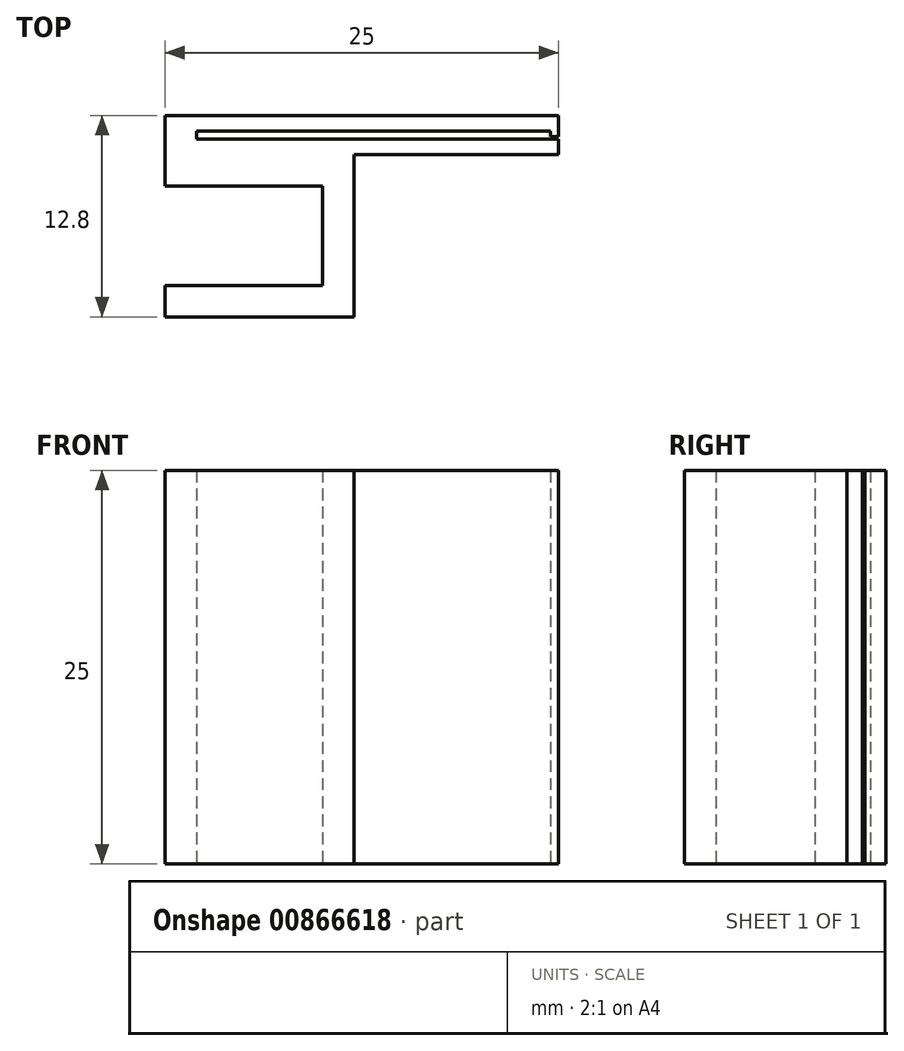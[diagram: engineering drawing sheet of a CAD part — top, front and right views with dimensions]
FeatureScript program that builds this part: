
annotation { "Feature Type Name" : "Feature", "Feature Type Description" : "" }
export const myFeature = defineFeature(function(context is Context, id is Id, definition is map)
    precondition{}
    {
        {
            var Q0;
            Q0=qCreatedBy(makeId("Top.planeOp"),FACE);
            var sketch = newSketch(context, id + "F0", { "sketchPlane" : qUnion([Q0])});
            skLineSegment(sketch, "E0.bottom", {"start": v(-10, 5.15) * mm, "end": v(2, 5.15) * mm});
            skLineSegment(sketch, "E0.top", {"start": v(-10, 3.15) * mm, "end": v(2, 3.15) * mm});
            skLineSegment(sketch, "E0.left", {"start": v(-10, 5.15) * mm, "end": v(-10, 3.15) * mm});
            skLineSegment(sketch, "E0.right", {"start": v(2, 5.15) * mm, "end": v(2, 3.15) * mm});
            skLineSegment(sketch, "E1.bottom", {"start": v(-10, -3.15) * mm, "end": v(2, -3.15) * mm});
            skLineSegment(sketch, "E1.top", {"start": v(-10, -5.15) * mm, "end": v(2, -5.15) * mm});
            skLineSegment(sketch, "E1.left", {"start": v(-10, -3.15) * mm, "end": v(-10, -5.15) * mm});
            skLineSegment(sketch, "E1.right", {"start": v(2, -3.15) * mm, "end": v(2, -5.15) * mm});
            skLineSegment(sketch, "E2.bottom", {"start": v(0, 3.15) * mm, "end": v(2, 3.15) * mm});
            skLineSegment(sketch, "E2.top", {"start": v(0, -3.15) * mm, "end": v(2, -3.15) * mm});
            skLineSegment(sketch, "E2.left", {"start": v(0, 3.15) * mm, "end": v(0, -3.15) * mm});
            skLineSegment(sketch, "E2.right", {"start": v(2, 3.15) * mm, "end": v(2, -3.15) * mm});
            skLineSegment(sketch, "E3", {"start": v(-10, 5.15) * mm, "end": v(15, 5.15) * mm});
            skLineSegment(sketch, "E4", {"start": v(15, 5.15) * mm, "end": v(15, 6.15) * mm});
            skLineSegment(sketch, "E5", {"start": v(15, 6.15) * mm, "end": v(-10, 6.15) * mm});
            skLineSegment(sketch, "E6", {"start": v(-10, 6.15) * mm, "end": v(-10, 5.15) * mm});
            skLineSegment(sketch, "E7.bottom", {"start": v(-10, 6.15) * mm, "end": v(-8, 6.15) * mm});
            skLineSegment(sketch, "E7.top", {"start": v(-10, 6.65) * mm, "end": v(-8, 6.65) * mm});
            skLineSegment(sketch, "E7.left", {"start": v(-10, 6.15) * mm, "end": v(-10, 6.65) * mm});
            skLineSegment(sketch, "E7.right", {"start": v(-8, 6.15) * mm, "end": v(-8, 6.65) * mm});
            skLineSegment(sketch, "E8.bottom", {"start": v(-10, 6.65) * mm, "end": v(15, 6.65) * mm});
            skLineSegment(sketch, "E8.top", {"start": v(-10, 7.65) * mm, "end": v(15, 7.65) * mm});
            skLineSegment(sketch, "E8.left", {"start": v(-10, 6.65) * mm, "end": v(-10, 7.65) * mm});
            skLineSegment(sketch, "E8.right", {"start": v(15, 6.65) * mm, "end": v(15, 7.65) * mm});
            skLineSegment(sketch, "E9.bottom", {"start": v(15, 6.65) * mm, "end": v(14.5, 6.65) * mm});
            skLineSegment(sketch, "E9.top", {"start": v(15, 6.3) * mm, "end": v(14.5, 6.3) * mm});
            skLineSegment(sketch, "E9.left", {"start": v(15, 6.65) * mm, "end": v(15, 6.3) * mm});
            skLineSegment(sketch, "E9.right", {"start": v(14.5, 6.65) * mm, "end": v(14.5, 6.3) * mm});
            skSolve(sketch);
        }
        {
            var Q0;
            Q0=qSketchRegion(id+"F0",true);
            extrude(context, id + "F1", {"entities" : qUnion([Q0]), "depth" : 25 * mm, "offsetDistance" : 25 * mm});
        }
    });
